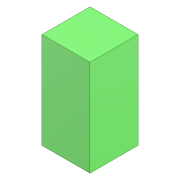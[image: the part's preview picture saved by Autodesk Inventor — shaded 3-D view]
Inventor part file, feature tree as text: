
AUTODESK INVENTOR PART (.ipt)
format: ipt  version: 2022 (Build 260153000, 153)  size: 101,888 bytes
history: native  units: mm
features: extrude x1, shell x1, fillet x1, sketch x1
ambient origin geometry x8: Origin, YZ Plane, XZ Plane, XY Plane, X Axis, Y Axis, Z Axis, Center Point
bodies: Solid1 (feature_tree)
feature tree (4):
  extrude  "Extrusion1"  Depth=50.0mm
  shell  "Shell1"  Thickness=100.0mm
  fillet  "Fillet1"  Radius=5.0mm
  sketch  "Sketch1"  dims[d0=50.0mm d1=50.0mm d2=100.0mm d3=0.0mm d4=5.0mm d5=19.0mm]
